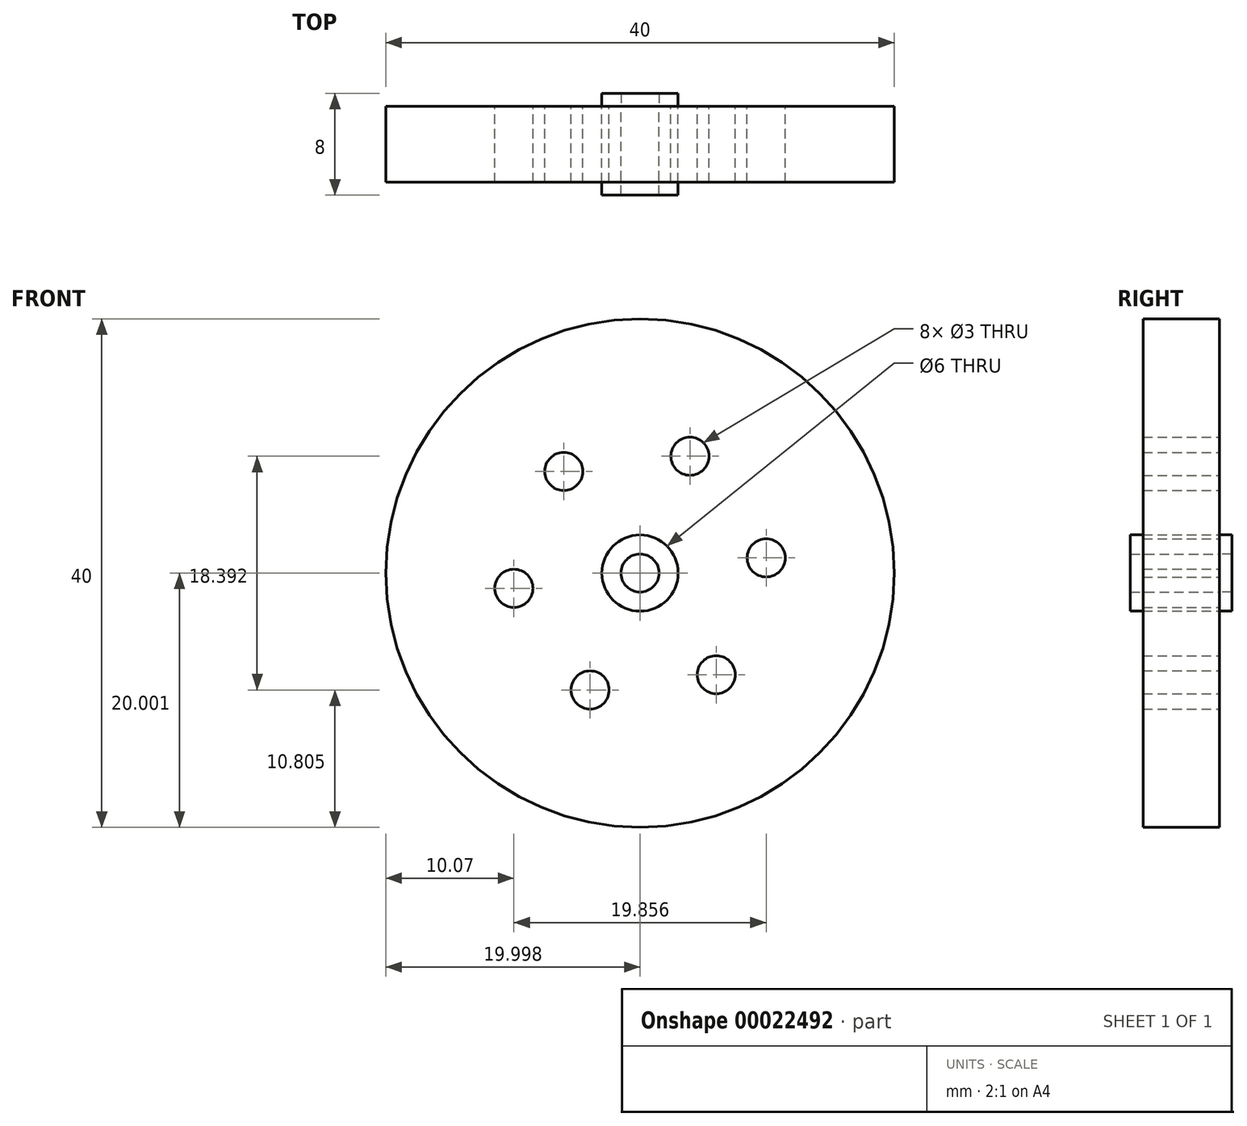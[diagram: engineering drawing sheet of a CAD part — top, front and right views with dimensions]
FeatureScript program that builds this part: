
annotation { "Feature Type Name" : "Feature", "Feature Type Description" : "" }
export const myFeature = defineFeature(function(context is Context, id is Id, definition is map)
    precondition{}
    {
        {
            var Q0;
            Q0=qCreatedBy(makeId("Front.planeOp"),FACE);
            var sketch = newSketch(context, id + "F0", { "sketchPlane" : qUnion([Q0])});
            skCircle(sketch, "E0", {"center": v(-7.15, 10.28) * mm, "radius": 20 * mm});
            skCircle(sketch, "E1", {"center": v(-7.15, 10.28) * mm, "radius": 1.5 * mm});
            skCircle(sketch, "E2", {"center": v(-7.15, 10.28) * mm, "radius": 3 * mm});
            skCircle(sketch, "E3", {"center": v(-13.15, 18.28) * mm, "radius": 1.5 * mm});
            skPoint(sketch, "E4.orphan", {"position": v(-19.15, 26.28) * mm});
            skCircle(sketch, "E5.1.0", {"center": v(-17.08, 9.08) * mm, "radius": 1.5 * mm});
            skCircle(sketch, "E5.2.0", {"center": v(-11.08, 1.08) * mm, "radius": 1.5 * mm});
            skCircle(sketch, "E5.3.0", {"center": v(-1.15, 2.28) * mm, "radius": 1.5 * mm});
            skCircle(sketch, "E5.4.0", {"center": v(2.78, 11.48) * mm, "radius": 1.5 * mm});
            skCircle(sketch, "E5.5.0", {"center": v(-3.22, 19.48) * mm, "radius": 1.5 * mm});
            skSolve(sketch);
        }
        {
            var Q0;
            Q0 = qSketchRegion(id + "F0", true);
            extrude(context, id + "F1", {"entities" : qUnion([Q0]), "depth" : 6 * mm});
        }
        {
            var Q0;
            Q0=makeQuery(id+"F1.opExtrude","CAP_FACE",FACE,{"disambiguationData":[OSD([sQuery(id+"F0.wireOp",EDGE,"E0"),sQuery(id+"F0.wireOp",EDGE,"E2"),sQuery(id+"F0.wireOp",EDGE,"E3"),sQuery(id+"F0.wireOp",EDGE,"E5.1.0"),sQuery(id+"F0.wireOp",EDGE,"E5.2.0"),sQuery(id+"F0.wireOp",EDGE,"E5.3.0"),sQuery(id+"F0.wireOp",EDGE,"E5.4.0"),sQuery(id+"F0.wireOp",EDGE,"E5.5.0")])],"isStart":true});
            var sketch = newSketch(context, id + "F2", { "sketchPlane" : qUnion([Q0])});
            skCircle(sketch, "E6", {"center": v(7.15, 10.28) * mm, "radius": 1.5 * mm});
            skSolve(sketch);
        }
        {
            var Q0;
            Q0=makeQuery(id+"F2.imprint","IMPRINT",FACE,{"disambiguationData":[TD([[makeQuery(id+"F2.imprint","IMPRINT",EDGE,{"derivedFrom":sQuery(id+"F2.wireOp",EDGE,"E6")}),-1.0]])]});
            extrude(context, id + "F3", {"entities" : qUnion([Q0]), "depth" : 1 * mm});
        }
        {
            var Q0;
            Q0=makeQuery(id+"F3.opExtrude","CAP_FACE",FACE,{"disambiguationData":[OSD([sQuery(id+"F0.wireOp",EDGE,"E2"),sQuery(id+"F2.wireOp",EDGE,"E6")])],"isStart":true});
            extrude(context, id + "F4", {"entities" : qUnion([Q0]), "depth" : 7 * mm});
        }
    });
